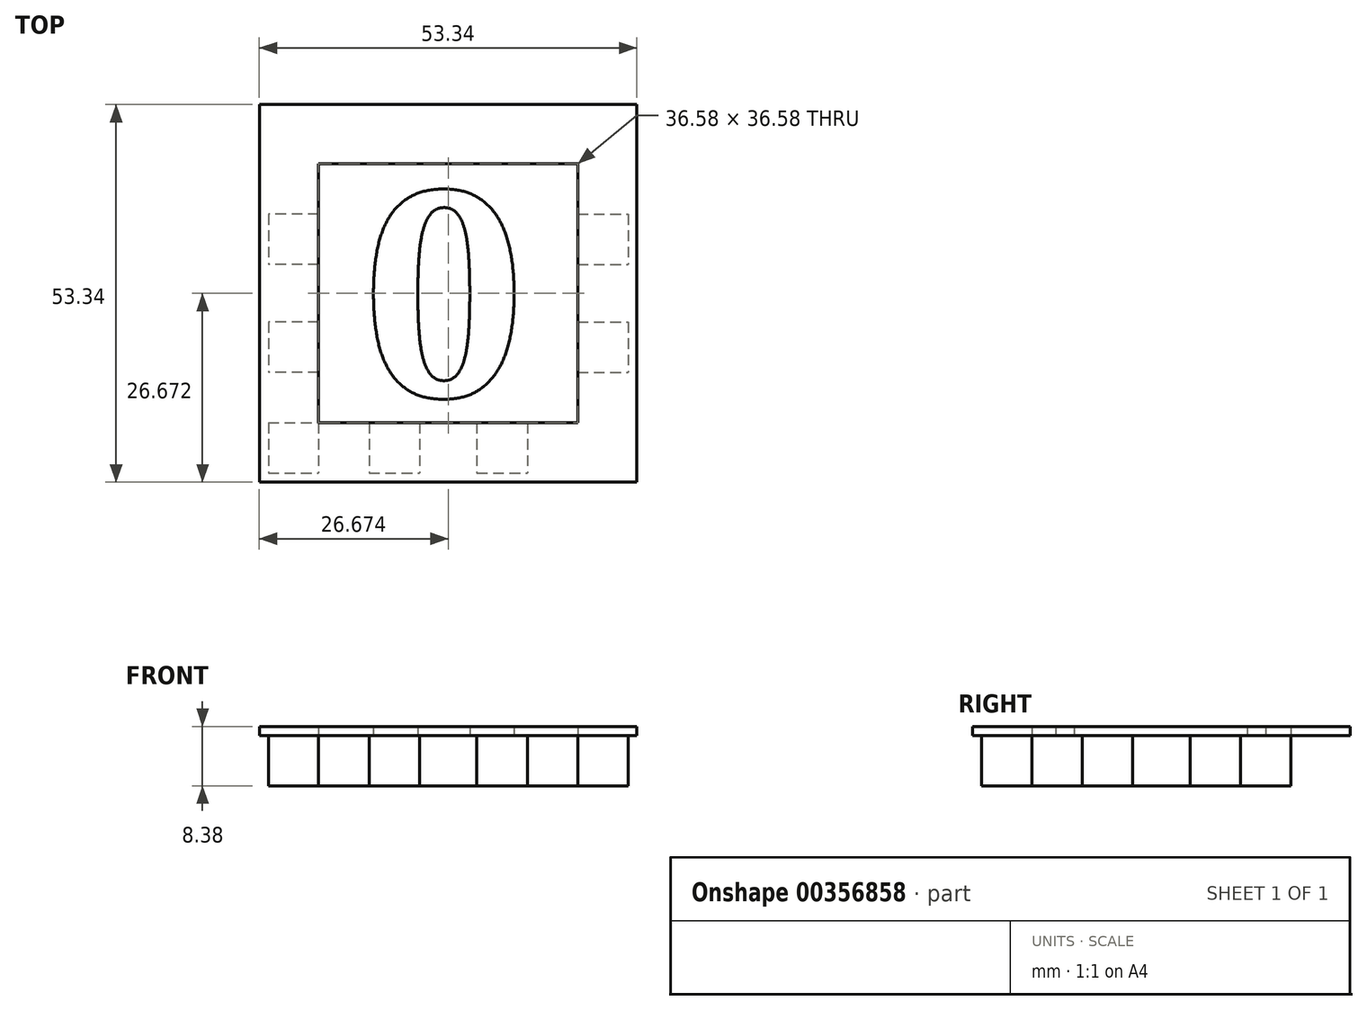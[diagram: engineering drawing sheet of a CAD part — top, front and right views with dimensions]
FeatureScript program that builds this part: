
annotation { "Feature Type Name" : "Feature", "Feature Type Description" : "" }
export const myFeature = defineFeature(function(context is Context, id is Id, definition is map)
    precondition{}
    {
        {
            var Q0;
            Q0=qCreatedBy(makeId("Top.planeOp"),FACE);
            var sketch = newSketch(context, id + "F0", { "sketchPlane" : qUnion([Q0])});
            skLineSegment(sketch, "E0.bottom", {"start": v(-28.29, 26.77) * mm, "end": v(15.4, 26.77) * mm});
            skLineSegment(sketch, "E0.top", {"start": v(-28.29, -24.03) * mm, "end": v(15.4, -24.03) * mm});
            skLineSegment(sketch, "E0.left", {"start": v(-28.29, 26.77) * mm, "end": v(-28.29, -24.03) * mm});
            skLineSegment(sketch, "E0.right", {"start": v(15.4, 26.77) * mm, "end": v(15.4, -24.03) * mm});
            skLineSegment(sketch, "E1.bottom", {"start": v(-28.29, 26.77) * mm, "end": v(-21.17, 26.77) * mm});
            skLineSegment(sketch, "E1.top", {"start": v(-28.29, 19.66) * mm, "end": v(-21.17, 19.66) * mm});
            skLineSegment(sketch, "E1.left", {"start": v(-28.29, 26.77) * mm, "end": v(-28.29, 19.66) * mm});
            skLineSegment(sketch, "E1.right", {"start": v(-21.17, 26.77) * mm, "end": v(-21.17, 19.66) * mm});
            skLineSegment(sketch, "E2.bottom", {"start": v(-21.17, 26.77) * mm, "end": v(-14.06, 26.77) * mm});
            skLineSegment(sketch, "E2.top", {"start": v(-21.17, 19.66) * mm, "end": v(-14.06, 19.66) * mm});
            skLineSegment(sketch, "E2.right", {"start": v(-14.06, 26.77) * mm, "end": v(-14.06, 19.66) * mm});
            skLineSegment(sketch, "E3.bottom", {"start": v(-14.06, 26.77) * mm, "end": v(-6.95, 26.77) * mm});
            skLineSegment(sketch, "E3.top", {"start": v(-14.06, 19.66) * mm, "end": v(-6.95, 19.66) * mm});
            skLineSegment(sketch, "E3.right", {"start": v(-6.95, 26.77) * mm, "end": v(-6.95, 19.66) * mm});
            skLineSegment(sketch, "E4.bottom", {"start": v(-6.95, 26.77) * mm, "end": v(1.18, 26.77) * mm});
            skLineSegment(sketch, "E4.top", {"start": v(-6.95, 19.66) * mm, "end": v(1.18, 19.66) * mm});
            skLineSegment(sketch, "E4.right", {"start": v(1.18, 26.77) * mm, "end": v(1.18, 19.66) * mm});
            skLineSegment(sketch, "E5.bottom", {"start": v(1.18, 26.77) * mm, "end": v(8.3, 26.77) * mm});
            skLineSegment(sketch, "E5.top", {"start": v(1.18, 19.66) * mm, "end": v(8.3, 19.66) * mm});
            skLineSegment(sketch, "E5.right", {"start": v(8.3, 26.77) * mm, "end": v(8.3, 19.66) * mm});
            skLineSegment(sketch, "E6.bottom", {"start": v(8.3, 26.77) * mm, "end": v(22.51, 26.77) * mm});
            skLineSegment(sketch, "E6.top", {"start": v(8.3, 19.66) * mm, "end": v(22.51, 19.66) * mm});
            skLineSegment(sketch, "E6.right", {"start": v(22.51, 26.77) * mm, "end": v(22.51, 19.66) * mm});
            skLineSegment(sketch, "E7.bottom", {"start": v(15.4, 26.77) * mm, "end": v(22.51, 26.77) * mm});
            skLineSegment(sketch, "E7.top", {"start": v(15.4, 19.66) * mm, "end": v(22.51, 19.66) * mm});
            skLineSegment(sketch, "E7.right", {"start": v(15.4, 26.77) * mm, "end": v(15.4, 19.66) * mm});
            skLineSegment(sketch, "E8.top", {"start": v(15.4, 12.55) * mm, "end": v(22.51, 12.55) * mm});
            skLineSegment(sketch, "E8.left", {"start": v(22.51, 19.66) * mm, "end": v(22.51, 12.55) * mm});
            skLineSegment(sketch, "E8.right", {"start": v(15.4, 19.66) * mm, "end": v(15.4, 12.55) * mm});
            skLineSegment(sketch, "E9.top", {"start": v(15.4, 5.44) * mm, "end": v(22.51, 5.44) * mm});
            skLineSegment(sketch, "E9.left", {"start": v(22.51, 12.55) * mm, "end": v(22.51, 5.44) * mm});
            skLineSegment(sketch, "E9.right", {"start": v(15.4, 12.55) * mm, "end": v(15.4, 5.44) * mm});
            skLineSegment(sketch, "E10.top", {"start": v(15.4, -2.7) * mm, "end": v(22.51, -2.7) * mm});
            skLineSegment(sketch, "E10.left", {"start": v(22.51, 5.44) * mm, "end": v(22.51, -2.7) * mm});
            skLineSegment(sketch, "E10.right", {"start": v(15.4, 5.44) * mm, "end": v(15.4, -2.7) * mm});
            skLineSegment(sketch, "E11.top", {"start": v(15.4, -9.8) * mm, "end": v(22.51, -9.8) * mm});
            skLineSegment(sketch, "E11.left", {"start": v(22.51, -2.7) * mm, "end": v(22.51, -9.8) * mm});
            skLineSegment(sketch, "E11.right", {"start": v(15.4, -2.7) * mm, "end": v(15.4, -9.8) * mm});
            skLineSegment(sketch, "E12.top", {"start": v(15.4, -16.92) * mm, "end": v(22.51, -16.92) * mm});
            skLineSegment(sketch, "E12.left", {"start": v(22.51, -9.8) * mm, "end": v(22.51, -16.92) * mm});
            skLineSegment(sketch, "E12.right", {"start": v(15.4, -9.8) * mm, "end": v(15.4, -16.92) * mm});
            skLineSegment(sketch, "E13.top", {"start": v(15.4, -24.03) * mm, "end": v(22.51, -24.03) * mm});
            skLineSegment(sketch, "E13.left", {"start": v(22.51, -16.92) * mm, "end": v(22.51, -24.03) * mm});
            skLineSegment(sketch, "E13.right", {"start": v(15.4, -16.92) * mm, "end": v(15.4, -24.03) * mm});
            skLineSegment(sketch, "E14.bottom", {"start": v(22.51, -16.92) * mm, "end": v(8.3, -16.92) * mm});
            skLineSegment(sketch, "E14.top", {"start": v(22.51, -24.03) * mm, "end": v(8.3, -24.03) * mm});
            skLineSegment(sketch, "E14.right", {"start": v(8.3, -16.92) * mm, "end": v(8.3, -24.03) * mm});
            skLineSegment(sketch, "E15.bottom", {"start": v(8.3, -16.92) * mm, "end": v(1.18, -16.92) * mm});
            skLineSegment(sketch, "E15.top", {"start": v(8.3, -24.03) * mm, "end": v(1.18, -24.03) * mm});
            skLineSegment(sketch, "E15.right", {"start": v(1.18, -16.92) * mm, "end": v(1.18, -24.03) * mm});
            skLineSegment(sketch, "E16.bottom", {"start": v(1.18, -16.92) * mm, "end": v(-6.95, -16.92) * mm});
            skLineSegment(sketch, "E16.top", {"start": v(1.18, -24.03) * mm, "end": v(-6.95, -24.03) * mm});
            skLineSegment(sketch, "E16.right", {"start": v(-6.95, -16.92) * mm, "end": v(-6.95, -24.03) * mm});
            skLineSegment(sketch, "E17.bottom", {"start": v(-6.95, -16.92) * mm, "end": v(-14.06, -16.92) * mm});
            skLineSegment(sketch, "E17.top", {"start": v(-6.95, -24.03) * mm, "end": v(-14.06, -24.03) * mm});
            skLineSegment(sketch, "E17.right", {"start": v(-14.06, -16.92) * mm, "end": v(-14.06, -24.03) * mm});
            skLineSegment(sketch, "E18.bottom", {"start": v(-21.17, 19.66) * mm, "end": v(-28.29, 19.66) * mm});
            skLineSegment(sketch, "E18.top", {"start": v(-21.17, 12.55) * mm, "end": v(-28.29, 12.55) * mm});
            skLineSegment(sketch, "E18.left", {"start": v(-21.17, 19.66) * mm, "end": v(-21.17, 12.55) * mm});
            skLineSegment(sketch, "E18.right", {"start": v(-28.29, 19.66) * mm, "end": v(-28.29, 12.55) * mm});
            skLineSegment(sketch, "E19.top", {"start": v(-21.17, 5.44) * mm, "end": v(-28.29, 5.44) * mm});
            skLineSegment(sketch, "E19.left", {"start": v(-21.17, 12.55) * mm, "end": v(-21.17, 5.44) * mm});
            skLineSegment(sketch, "E19.right", {"start": v(-28.29, 12.55) * mm, "end": v(-28.29, 5.44) * mm});
            skLineSegment(sketch, "E20.top", {"start": v(-21.17, -2.7) * mm, "end": v(-28.29, -2.7) * mm});
            skLineSegment(sketch, "E20.left", {"start": v(-21.17, 5.44) * mm, "end": v(-21.17, -2.7) * mm});
            skLineSegment(sketch, "E20.right", {"start": v(-28.29, 5.44) * mm, "end": v(-28.29, -2.7) * mm});
            skLineSegment(sketch, "E21.top", {"start": v(-21.17, -9.8) * mm, "end": v(-28.29, -9.8) * mm});
            skLineSegment(sketch, "E21.left", {"start": v(-21.17, -2.7) * mm, "end": v(-21.17, -9.8) * mm});
            skLineSegment(sketch, "E21.right", {"start": v(-28.29, -2.7) * mm, "end": v(-28.29, -9.8) * mm});
            skLineSegment(sketch, "E22.bottom", {"start": v(-28.29, -9.8) * mm, "end": v(-21.17, -9.8) * mm});
            skLineSegment(sketch, "E22.top", {"start": v(-28.29, -16.92) * mm, "end": v(-21.17, -16.92) * mm});
            skLineSegment(sketch, "E22.left", {"start": v(-28.29, -9.8) * mm, "end": v(-28.29, -16.92) * mm});
            skLineSegment(sketch, "E22.right", {"start": v(-21.17, -9.8) * mm, "end": v(-21.17, -16.92) * mm});
            skLineSegment(sketch, "E23.top", {"start": v(-28.29, -24.03) * mm, "end": v(-21.17, -24.03) * mm});
            skLineSegment(sketch, "E23.left", {"start": v(-28.29, -16.92) * mm, "end": v(-28.29, -24.03) * mm});
            skLineSegment(sketch, "E23.right", {"start": v(-21.17, -16.92) * mm, "end": v(-21.17, -24.03) * mm});
            skLineSegment(sketch, "E24.bottom", {"start": v(-21.17, -16.92) * mm, "end": v(-14.06, -16.92) * mm});
            skLineSegment(sketch, "E24.top", {"start": v(-21.17, -24.03) * mm, "end": v(-14.06, -24.03) * mm});
            skLineSegment(sketch, "E25.bottom", {"start": v(55.44, 26.09) * mm, "end": v(106.24, 26.09) * mm});
            skLineSegment(sketch, "E25.top", {"start": v(55.44, -24.71) * mm, "end": v(106.24, -24.71) * mm});
            skLineSegment(sketch, "E25.left", {"start": v(55.44, 26.09) * mm, "end": v(55.44, -24.71) * mm});
            skLineSegment(sketch, "E25.right", {"start": v(106.24, 26.09) * mm, "end": v(106.24, -24.71) * mm});
            skLineSegment(sketch, "E26.bottom", {"start": v(55.44, 26.09) * mm, "end": v(62.55, 26.09) * mm});
            skLineSegment(sketch, "E26.top", {"start": v(55.44, 18.97) * mm, "end": v(62.55, 18.97) * mm});
            skLineSegment(sketch, "E26.left", {"start": v(55.44, 26.09) * mm, "end": v(55.44, 18.97) * mm});
            skLineSegment(sketch, "E26.right", {"start": v(62.55, 26.09) * mm, "end": v(62.55, 18.97) * mm});
            skLineSegment(sketch, "E27.bottom", {"start": v(62.55, 26.09) * mm, "end": v(69.67, 26.09) * mm});
            skLineSegment(sketch, "E27.top", {"start": v(62.55, 18.97) * mm, "end": v(69.67, 18.97) * mm});
            skLineSegment(sketch, "E27.right", {"start": v(69.67, 26.09) * mm, "end": v(69.67, 18.97) * mm});
            skLineSegment(sketch, "E28.bottom", {"start": v(69.67, 26.09) * mm, "end": v(76.78, 26.09) * mm});
            skLineSegment(sketch, "E28.top", {"start": v(69.67, 18.97) * mm, "end": v(76.78, 18.97) * mm});
            skLineSegment(sketch, "E28.right", {"start": v(76.78, 26.09) * mm, "end": v(76.78, 18.97) * mm});
            skLineSegment(sketch, "E29.bottom", {"start": v(76.78, 26.09) * mm, "end": v(84.9, 26.09) * mm});
            skLineSegment(sketch, "E29.top", {"start": v(76.78, 18.97) * mm, "end": v(84.9, 18.97) * mm});
            skLineSegment(sketch, "E29.right", {"start": v(84.9, 26.09) * mm, "end": v(84.9, 18.97) * mm});
            skLineSegment(sketch, "E30.bottom", {"start": v(84.9, 26.09) * mm, "end": v(92.02, 26.09) * mm});
            skLineSegment(sketch, "E30.top", {"start": v(84.9, 18.97) * mm, "end": v(92.02, 18.97) * mm});
            skLineSegment(sketch, "E30.right", {"start": v(92.02, 26.09) * mm, "end": v(92.02, 18.97) * mm});
            skLineSegment(sketch, "E31.bottom", {"start": v(92.02, 26.09) * mm, "end": v(99.13, 26.09) * mm});
            skLineSegment(sketch, "E31.top", {"start": v(92.02, 18.97) * mm, "end": v(99.13, 18.97) * mm});
            skLineSegment(sketch, "E31.right", {"start": v(99.13, 26.09) * mm, "end": v(99.13, 18.97) * mm});
            skLineSegment(sketch, "E32.bottom", {"start": v(99.13, 26.09) * mm, "end": v(106.24, 26.09) * mm});
            skLineSegment(sketch, "E32.top", {"start": v(99.13, 18.97) * mm, "end": v(106.24, 18.97) * mm});
            skLineSegment(sketch, "E32.right", {"start": v(106.24, 26.09) * mm, "end": v(106.24, 18.97) * mm});
            skLineSegment(sketch, "E33.top", {"start": v(99.13, 11.86) * mm, "end": v(106.24, 11.86) * mm});
            skLineSegment(sketch, "E33.left", {"start": v(99.13, 18.97) * mm, "end": v(99.13, 11.86) * mm});
            skLineSegment(sketch, "E33.right", {"start": v(106.24, 18.97) * mm, "end": v(106.24, 11.86) * mm});
            skLineSegment(sketch, "E34.top", {"start": v(99.13, 4.75) * mm, "end": v(106.24, 4.75) * mm});
            skLineSegment(sketch, "E34.left", {"start": v(99.13, 11.86) * mm, "end": v(99.13, 4.75) * mm});
            skLineSegment(sketch, "E34.right", {"start": v(106.24, 11.86) * mm, "end": v(106.24, 4.75) * mm});
            skLineSegment(sketch, "E35.top", {"start": v(99.13, -3.38) * mm, "end": v(106.24, -3.38) * mm});
            skLineSegment(sketch, "E35.left", {"start": v(99.13, 4.75) * mm, "end": v(99.13, -3.38) * mm});
            skLineSegment(sketch, "E35.right", {"start": v(106.24, 4.75) * mm, "end": v(106.24, -3.38) * mm});
            skLineSegment(sketch, "E36.top", {"start": v(99.13, -10.49) * mm, "end": v(106.24, -10.49) * mm});
            skLineSegment(sketch, "E36.left", {"start": v(99.13, -3.38) * mm, "end": v(99.13, -10.49) * mm});
            skLineSegment(sketch, "E36.right", {"start": v(106.24, -3.38) * mm, "end": v(106.24, -10.49) * mm});
            skLineSegment(sketch, "E37.top", {"start": v(99.13, -17.6) * mm, "end": v(106.24, -17.6) * mm});
            skLineSegment(sketch, "E37.left", {"start": v(99.13, -10.49) * mm, "end": v(99.13, -17.6) * mm});
            skLineSegment(sketch, "E37.right", {"start": v(106.24, -10.49) * mm, "end": v(106.24, -17.6) * mm});
            skLineSegment(sketch, "E38.top", {"start": v(99.13, -24.71) * mm, "end": v(106.24, -24.71) * mm});
            skLineSegment(sketch, "E38.left", {"start": v(99.13, -17.6) * mm, "end": v(99.13, -24.71) * mm});
            skLineSegment(sketch, "E38.right", {"start": v(106.24, -17.6) * mm, "end": v(106.24, -24.71) * mm});
            skLineSegment(sketch, "E39.bottom", {"start": v(99.13, -17.6) * mm, "end": v(92.02, -17.6) * mm});
            skLineSegment(sketch, "E39.top", {"start": v(99.13, -24.71) * mm, "end": v(92.02, -24.71) * mm});
            skLineSegment(sketch, "E39.right", {"start": v(92.02, -17.6) * mm, "end": v(92.02, -24.71) * mm});
            skLineSegment(sketch, "E40.bottom", {"start": v(92.02, -17.6) * mm, "end": v(84.9, -17.6) * mm});
            skLineSegment(sketch, "E40.top", {"start": v(92.02, -24.71) * mm, "end": v(84.9, -24.71) * mm});
            skLineSegment(sketch, "E40.right", {"start": v(84.9, -17.6) * mm, "end": v(84.9, -24.71) * mm});
            skLineSegment(sketch, "E41.bottom", {"start": v(84.9, -17.6) * mm, "end": v(76.78, -17.6) * mm});
            skLineSegment(sketch, "E41.top", {"start": v(84.9, -24.71) * mm, "end": v(76.78, -24.71) * mm});
            skLineSegment(sketch, "E41.right", {"start": v(76.78, -17.6) * mm, "end": v(76.78, -24.71) * mm});
            skLineSegment(sketch, "E42.bottom", {"start": v(76.78, -17.6) * mm, "end": v(69.67, -17.6) * mm});
            skLineSegment(sketch, "E42.top", {"start": v(76.78, -24.71) * mm, "end": v(69.67, -24.71) * mm});
            skLineSegment(sketch, "E42.right", {"start": v(69.67, -17.6) * mm, "end": v(69.67, -24.71) * mm});
            skLineSegment(sketch, "E43.bottom", {"start": v(62.55, 18.97) * mm, "end": v(55.44, 18.97) * mm});
            skLineSegment(sketch, "E43.top", {"start": v(62.55, 11.86) * mm, "end": v(55.44, 11.86) * mm});
            skLineSegment(sketch, "E43.left", {"start": v(62.55, 18.97) * mm, "end": v(62.55, 11.86) * mm});
            skLineSegment(sketch, "E43.right", {"start": v(55.44, 18.97) * mm, "end": v(55.44, 11.86) * mm});
            skLineSegment(sketch, "E44.top", {"start": v(62.55, 4.75) * mm, "end": v(55.44, 4.75) * mm});
            skLineSegment(sketch, "E44.left", {"start": v(62.55, 11.86) * mm, "end": v(62.55, 4.75) * mm});
            skLineSegment(sketch, "E44.right", {"start": v(55.44, 11.86) * mm, "end": v(55.44, 4.75) * mm});
            skLineSegment(sketch, "E45.top", {"start": v(62.55, -3.38) * mm, "end": v(55.44, -3.38) * mm});
            skLineSegment(sketch, "E45.left", {"start": v(62.55, 4.75) * mm, "end": v(62.55, -3.38) * mm});
            skLineSegment(sketch, "E45.right", {"start": v(55.44, 4.75) * mm, "end": v(55.44, -3.38) * mm});
            skLineSegment(sketch, "E46.top", {"start": v(62.55, -10.49) * mm, "end": v(55.44, -10.49) * mm});
            skLineSegment(sketch, "E46.left", {"start": v(62.55, -3.38) * mm, "end": v(62.55, -10.49) * mm});
            skLineSegment(sketch, "E46.right", {"start": v(55.44, -3.38) * mm, "end": v(55.44, -10.49) * mm});
            skLineSegment(sketch, "E47.top", {"start": v(62.55, -17.6) * mm, "end": v(55.44, -17.6) * mm});
            skLineSegment(sketch, "E47.left", {"start": v(62.55, -10.49) * mm, "end": v(62.55, -17.6) * mm});
            skLineSegment(sketch, "E47.right", {"start": v(55.44, -10.49) * mm, "end": v(55.44, -17.6) * mm});
            skLineSegment(sketch, "E48.bottom", {"start": v(62.55, -17.6) * mm, "end": v(69.67, -17.6) * mm});
            skLineSegment(sketch, "E48.top", {"start": v(62.55, -24.71) * mm, "end": v(69.67, -24.71) * mm});
            skLineSegment(sketch, "E48.left", {"start": v(62.55, -17.6) * mm, "end": v(62.55, -24.71) * mm});
            skLineSegment(sketch, "E49.top", {"start": v(62.55, -24.71) * mm, "end": v(55.44, -24.71) * mm});
            skLineSegment(sketch, "E49.right", {"start": v(55.44, -17.6) * mm, "end": v(55.44, -24.71) * mm});
            skSolve(sketch);
        }
        {
            var Q0;
            Q0=makeQuery(id+"F0.imprint","IMPRINT",FACE,{"disambiguationData":[TD([[makeQuery(id+"F0.imprint","IMPRINT",EDGE,{"derivedFrom":sQuery(id+"F0.wireOp",EDGE,"E1.bottom")}),-1.0]])]});
            var Q1;
            Q1=makeQuery(id+"F0.imprint","IMPRINT",FACE,{"disambiguationData":[TD([[makeQuery(id+"F0.imprint","IMPRINT",EDGE,{"derivedFrom":sQuery(id+"F0.wireOp",EDGE,"E3.bottom")}),-1.0]])]});
            var Q2;
            Q2=makeQuery(id+"F0.imprint","IMPRINT",FACE,{"disambiguationData":[TD([[makeQuery(id+"F0.imprint","IMPRINT",EDGE,{"derivedFrom":sQuery(id+"F0.wireOp",EDGE,"E5.bottom")}),-1.0]])]});
            var Q3;
            Q3=makeQuery(id+"F0.imprint","IMPRINT",FACE,{"disambiguationData":[TD([[makeQuery(id+"F0.imprint","IMPRINT",EDGE,{"derivedFrom":sQuery(id+"F0.wireOp",EDGE,"E7.bottom")}),-1.0]])]});
            var Q4;
            Q4=makeQuery(id+"F0.imprint","IMPRINT",FACE,{"disambiguationData":[TD([[makeQuery(id+"F0.imprint","IMPRINT",EDGE,{"derivedFrom":sQuery(id+"F0.wireOp",EDGE,"E8.top")}),-1.0]])]});
            var Q5;
            Q5=makeQuery(id+"F0.imprint","IMPRINT",FACE,{"disambiguationData":[TD([[makeQuery(id+"F0.imprint","IMPRINT",EDGE,{"derivedFrom":sQuery(id+"F0.wireOp",EDGE,"E10.top")}),-1.0]])]});
            var Q6;
            {var subQ0=sQuery(id+"F0.wireOp",EDGE,"E13.right");Q6=makeQuery(id+"F0.imprint","IMPRINT",FACE,{"disambiguationData":[TD([[makeQuery(id+"F0.imprint","IMPRINT",EDGE,{"derivedFrom":subQ0}),1.0]])]});}
            var Q7;
            Q7=makeQuery(id+"F0.imprint","IMPRINT",FACE,{"disambiguationData":[TD([[makeQuery(id+"F0.imprint","IMPRINT",EDGE,{"derivedFrom":sQuery(id+"F0.wireOp",EDGE,"E15.bottom")}),1.0]])]});
            var Q8;
            Q8=makeQuery(id+"F0.imprint","IMPRINT",FACE,{"disambiguationData":[TD([[makeQuery(id+"F0.imprint","IMPRINT",EDGE,{"derivedFrom":sQuery(id+"F0.wireOp",EDGE,"E2.top")}),-1.0]])]});
            var Q9;
            Q9=makeQuery(id+"F0.imprint","IMPRINT",FACE,{"disambiguationData":[TD([[makeQuery(id+"F0.imprint","IMPRINT",EDGE,{"derivedFrom":sQuery(id+"F0.wireOp",EDGE,"E17.bottom")}),1.0]])]});
            var Q10;
            Q10=makeQuery(id+"F0.imprint","IMPRINT",FACE,{"disambiguationData":[TD([[makeQuery(id+"F0.imprint","IMPRINT",EDGE,{"derivedFrom":sQuery(id+"F0.wireOp",EDGE,"E22.top")}),-1.0]])]});
            var Q11;
            Q11=makeQuery(id+"F0.imprint","IMPRINT",FACE,{"disambiguationData":[TD([[makeQuery(id+"F0.imprint","IMPRINT",EDGE,{"derivedFrom":sQuery(id+"F0.wireOp",EDGE,"E20.top")}),1.0]])]});
            var Q12;
            Q12=makeQuery(id+"F0.imprint","IMPRINT",FACE,{"disambiguationData":[TD([[makeQuery(id+"F0.imprint","IMPRINT",EDGE,{"derivedFrom":sQuery(id+"F0.wireOp",EDGE,"E18.top")}),1.0]])]});
            var Q13;
            Q13=makeQuery(id+"F0.imprint","IMPRINT",FACE,{"disambiguationData":[TD([[makeQuery(id+"F0.imprint","IMPRINT",EDGE,{"derivedFrom":sQuery(id+"F0.wireOp",EDGE,"E27.top")}),-1.0]])]});
            var Q14;
            Q14=makeQuery(id+"F0.imprint","IMPRINT",FACE,{"disambiguationData":[TD([[makeQuery(id+"F0.imprint","IMPRINT",EDGE,{"derivedFrom":sQuery(id+"F0.wireOp",EDGE,"E31.bottom")}),-1.0]])]});
            var Q15;
            Q15=makeQuery(id+"F0.imprint","IMPRINT",FACE,{"disambiguationData":[TD([[makeQuery(id+"F0.imprint","IMPRINT",EDGE,{"derivedFrom":sQuery(id+"F0.wireOp",EDGE,"E29.bottom")}),-1.0]])]});
            var Q16;
            Q16=makeQuery(id+"F0.imprint","IMPRINT",FACE,{"disambiguationData":[TD([[makeQuery(id+"F0.imprint","IMPRINT",EDGE,{"derivedFrom":sQuery(id+"F0.wireOp",EDGE,"E43.bottom")}),1.0]])]});
            var Q17;
            Q17=makeQuery(id+"F0.imprint","IMPRINT",FACE,{"disambiguationData":[TD([[makeQuery(id+"F0.imprint","IMPRINT",EDGE,{"derivedFrom":sQuery(id+"F0.wireOp",EDGE,"E44.top")}),1.0]])]});
            var Q18;
            Q18=makeQuery(id+"F0.imprint","IMPRINT",FACE,{"disambiguationData":[TD([[makeQuery(id+"F0.imprint","IMPRINT",EDGE,{"derivedFrom":sQuery(id+"F0.wireOp",EDGE,"E36.top")}),-1.0]])]});
            var Q19;
            Q19=makeQuery(id+"F0.imprint","IMPRINT",FACE,{"disambiguationData":[TD([[makeQuery(id+"F0.imprint","IMPRINT",EDGE,{"derivedFrom":sQuery(id+"F0.wireOp",EDGE,"E34.top")}),-1.0]])]});
            var Q20;
            Q20=makeQuery(id+"F0.imprint","IMPRINT",FACE,{"disambiguationData":[TD([[makeQuery(id+"F0.imprint","IMPRINT",EDGE,{"derivedFrom":sQuery(id+"F0.wireOp",EDGE,"E46.top")}),1.0]])]});
            var Q21;
            Q21=makeQuery(id+"F0.imprint","IMPRINT",FACE,{"disambiguationData":[TD([[makeQuery(id+"F0.imprint","IMPRINT",EDGE,{"derivedFrom":sQuery(id+"F0.wireOp",EDGE,"E32.top")}),-1.0]])]});
            var Q22;
            Q22=makeQuery(id+"F0.imprint","IMPRINT",FACE,{"disambiguationData":[TD([[makeQuery(id+"F0.imprint","IMPRINT",EDGE,{"derivedFrom":sQuery(id+"F0.wireOp",EDGE,"E27.bottom")}),-1.0]])]});
            var Q23;
            Q23=makeQuery(id+"F0.imprint","IMPRINT",FACE,{"disambiguationData":[TD([[makeQuery(id+"F0.imprint","IMPRINT",EDGE,{"derivedFrom":sQuery(id+"F0.wireOp",EDGE,"E42.bottom")}),1.0]])]});
            var Q24;
            Q24=makeQuery(id+"F0.imprint","IMPRINT",FACE,{"disambiguationData":[TD([[makeQuery(id+"F0.imprint","IMPRINT",EDGE,{"derivedFrom":sQuery(id+"F0.wireOp",EDGE,"E40.bottom")}),1.0]])]});
            extrude(context, id + "F1", {"entities" : qUnion([Q0, Q1, Q2, Q3, Q4, Q5, Q6, Q7, Q8, Q9, Q10, Q11, Q12, Q13, Q14, Q15, Q16, Q17, Q18, Q19, Q20, Q21, Q22, Q23, Q24]), "depth" : 7.11 * mm});
        }
        {
            var Q0;
            Q0=makeQuery(id+"F1.opExtrude","CAP_FACE",FACE,{"disambiguationData":[OSD([sQuery(id+"F0.wireOp",EDGE,"E2.top"),sQuery(id+"F0.wireOp",EDGE,"E3.bottom"),sQuery(id+"F0.wireOp",EDGE,"E2.right"),sQuery(id+"F0.wireOp",EDGE,"E4.top"),sQuery(id+"F0.wireOp",EDGE,"E3.right"),sQuery(id+"F0.wireOp",EDGE,"E5.bottom"),sQuery(id+"F0.wireOp",EDGE,"E4.right"),sQuery(id+"F0.wireOp",EDGE,"E6.top"),sQuery(id+"F0.wireOp",EDGE,"E5.right"),sQuery(id+"F0.wireOp",EDGE,"E8.right"),sQuery(id+"F0.wireOp",EDGE,"E8.top"),sQuery(id+"F0.wireOp",EDGE,"E9.left"),sQuery(id+"F0.wireOp",EDGE,"E9.top"),sQuery(id+"F0.wireOp",EDGE,"E10.right"),sQuery(id+"F0.wireOp",EDGE,"E10.top"),sQuery(id+"F0.wireOp",EDGE,"E11.left"),sQuery(id+"F0.wireOp",EDGE,"E11.top"),sQuery(id+"F0.wireOp",EDGE,"E12.right"),sQuery(id+"F0.wireOp",EDGE,"E14.bottom"),sQuery(id+"F0.wireOp",EDGE,"E15.top"),sQuery(id+"F0.wireOp",EDGE,"E14.right"),sQuery(id+"F0.wireOp",EDGE,"E16.bottom"),sQuery(id+"F0.wireOp",EDGE,"E15.right"),sQuery(id+"F0.wireOp",EDGE,"E17.top"),sQuery(id+"F0.wireOp",EDGE,"E16.right"),sQuery(id+"F0.wireOp",EDGE,"E18.left"),sQuery(id+"F0.wireOp",EDGE,"E18.top"),sQuery(id+"F0.wireOp",EDGE,"E19.right"),sQuery(id+"F0.wireOp",EDGE,"E19.top"),sQuery(id+"F0.wireOp",EDGE,"E20.left"),sQuery(id+"F0.wireOp",EDGE,"E20.top"),sQuery(id+"F0.wireOp",EDGE,"E21.right"),sQuery(id+"F0.wireOp",EDGE,"E22.bottom"),sQuery(id+"F0.wireOp",EDGE,"E22.right"),sQuery(id+"F0.wireOp",EDGE,"E24.bottom"),sQuery(id+"F0.wireOp",EDGE,"E17.right")])],"isStart":false});
            var sketch = newSketch(context, id + "F2", { "sketchPlane" : qUnion([Q0])});
            skLineSegment(sketch, "E50.bottom", {"start": v(-29.56, -25.3) * mm, "end": v(23.78, -25.3) * mm});
            skLineSegment(sketch, "E50.top", {"start": v(-29.56, -16.92) * mm, "end": v(23.78, -16.92) * mm});
            skLineSegment(sketch, "E50.left", {"start": v(-29.56, -25.3) * mm, "end": v(-29.56, -16.92) * mm});
            skLineSegment(sketch, "E50.right", {"start": v(23.78, -25.3) * mm, "end": v(23.78, -16.92) * mm});
            skLineSegment(sketch, "E51.bottom", {"start": v(-29.56, -25.3) * mm, "end": v(-21.17, -25.3) * mm});
            skLineSegment(sketch, "E51.top", {"start": v(-29.56, 28.04) * mm, "end": v(-21.17, 28.04) * mm});
            skLineSegment(sketch, "E51.left", {"start": v(-29.56, -25.3) * mm, "end": v(-29.56, 28.04) * mm});
            skLineSegment(sketch, "E51.right", {"start": v(-21.17, -25.3) * mm, "end": v(-21.17, 28.04) * mm});
            skLineSegment(sketch, "E52.bottom", {"start": v(-29.56, 19.66) * mm, "end": v(23.78, 19.66) * mm});
            skLineSegment(sketch, "E52.top", {"start": v(-29.56, 28.04) * mm, "end": v(23.78, 28.04) * mm});
            skLineSegment(sketch, "E52.left", {"start": v(-29.56, 19.66) * mm, "end": v(-29.56, 28.04) * mm});
            skLineSegment(sketch, "E52.right", {"start": v(23.78, 19.66) * mm, "end": v(23.78, 28.04) * mm});
            skLineSegment(sketch, "E53.bottom", {"start": v(23.78, 28.04) * mm, "end": v(15.4, 28.04) * mm});
            skLineSegment(sketch, "E53.top", {"start": v(23.78, -25.3) * mm, "end": v(15.4, -25.3) * mm});
            skLineSegment(sketch, "E53.left", {"start": v(23.78, 28.04) * mm, "end": v(23.78, -25.3) * mm});
            skLineSegment(sketch, "E53.right", {"start": v(15.4, 28.04) * mm, "end": v(15.4, -25.3) * mm});
            skSolve(sketch);
        }
        {
            var Q0;
            Q0=qSketchRegion(id+"F2",true);
            extrude(context, id + "F3", {"entities" : qUnion([Q0]), "depth" : 1.27 * mm});
        }
        {
            var Q0;
            Q0=makeQuery(id+"F1.opExtrude","CAP_FACE",FACE,{"disambiguationData":[OSD([sQuery(id+"F0.wireOp",EDGE,"E27.bottom"),sQuery(id+"F0.wireOp",EDGE,"E26.right"),sQuery(id+"F0.wireOp",EDGE,"E28.top"),sQuery(id+"F0.wireOp",EDGE,"E27.right"),sQuery(id+"F0.wireOp",EDGE,"E29.bottom"),sQuery(id+"F0.wireOp",EDGE,"E28.right"),sQuery(id+"F0.wireOp",EDGE,"E30.top"),sQuery(id+"F0.wireOp",EDGE,"E29.right"),sQuery(id+"F0.wireOp",EDGE,"E31.bottom"),sQuery(id+"F0.wireOp",EDGE,"E30.right"),sQuery(id+"F0.wireOp",EDGE,"E31.right"),sQuery(id+"F0.wireOp",EDGE,"E32.top"),sQuery(id+"F0.wireOp",EDGE,"E33.right"),sQuery(id+"F0.wireOp",EDGE,"E33.top"),sQuery(id+"F0.wireOp",EDGE,"E34.left"),sQuery(id+"F0.wireOp",EDGE,"E34.top"),sQuery(id+"F0.wireOp",EDGE,"E35.right"),sQuery(id+"F0.wireOp",EDGE,"E35.top"),sQuery(id+"F0.wireOp",EDGE,"E36.left"),sQuery(id+"F0.wireOp",EDGE,"E36.top"),sQuery(id+"F0.wireOp",EDGE,"E37.right"),sQuery(id+"F0.wireOp",EDGE,"E37.top"),sQuery(id+"F0.wireOp",EDGE,"E39.bottom"),sQuery(id+"F0.wireOp",EDGE,"E40.top"),sQuery(id+"F0.wireOp",EDGE,"E39.right"),sQuery(id+"F0.wireOp",EDGE,"E41.bottom"),sQuery(id+"F0.wireOp",EDGE,"E40.right"),sQuery(id+"F0.wireOp",EDGE,"E42.top"),sQuery(id+"F0.wireOp",EDGE,"E41.right"),sQuery(id+"F0.wireOp",EDGE,"E43.bottom"),sQuery(id+"F0.wireOp",EDGE,"E43.right"),sQuery(id+"F0.wireOp",EDGE,"E43.top"),sQuery(id+"F0.wireOp",EDGE,"E44.left"),sQuery(id+"F0.wireOp",EDGE,"E44.top"),sQuery(id+"F0.wireOp",EDGE,"E45.right"),sQuery(id+"F0.wireOp",EDGE,"E45.top"),sQuery(id+"F0.wireOp",EDGE,"E46.left"),sQuery(id+"F0.wireOp",EDGE,"E46.top"),sQuery(id+"F0.wireOp",EDGE,"E47.right"),sQuery(id+"F0.wireOp",EDGE,"E48.bottom"),sQuery(id+"F0.wireOp",EDGE,"E42.right"),sQuery(id+"F0.wireOp",EDGE,"E47.top")])],"isStart":false});
            var sketch = newSketch(context, id + "F4", { "sketchPlane" : qUnion([Q0])});
            skLineSegment(sketch, "E54.bottom", {"start": v(55.44, -24.71) * mm, "end": v(62.55, -24.71) * mm});
            skLineSegment(sketch, "E54.top", {"start": v(55.44, 26.09) * mm, "end": v(62.55, 26.09) * mm});
            skLineSegment(sketch, "E54.left", {"start": v(55.44, -24.71) * mm, "end": v(55.44, 26.09) * mm});
            skLineSegment(sketch, "E54.right", {"start": v(62.55, -24.71) * mm, "end": v(62.55, 26.09) * mm});
            skLineSegment(sketch, "E55.bottom", {"start": v(55.44, -24.71) * mm, "end": v(106.24, -24.71) * mm});
            skLineSegment(sketch, "E55.top", {"start": v(55.44, -17.6) * mm, "end": v(106.24, -17.6) * mm});
            skLineSegment(sketch, "E55.left", {"start": v(55.44, -24.71) * mm, "end": v(55.44, -17.6) * mm});
            skLineSegment(sketch, "E55.right", {"start": v(106.24, -24.71) * mm, "end": v(106.24, -17.6) * mm});
            skLineSegment(sketch, "E56.bottom", {"start": v(106.24, -24.71) * mm, "end": v(99.13, -24.71) * mm});
            skLineSegment(sketch, "E56.top", {"start": v(106.24, 26.09) * mm, "end": v(99.13, 26.09) * mm});
            skLineSegment(sketch, "E56.left", {"start": v(106.24, -24.71) * mm, "end": v(106.24, 26.09) * mm});
            skLineSegment(sketch, "E56.right", {"start": v(99.13, -24.71) * mm, "end": v(99.13, 26.09) * mm});
            skLineSegment(sketch, "E57.bottom", {"start": v(106.24, 26.09) * mm, "end": v(55.44, 26.09) * mm});
            skLineSegment(sketch, "E57.top", {"start": v(106.24, 18.97) * mm, "end": v(55.44, 18.97) * mm});
            skLineSegment(sketch, "E57.left", {"start": v(106.24, 26.09) * mm, "end": v(106.24, 18.97) * mm});
            skLineSegment(sketch, "E57.right", {"start": v(55.44, 26.09) * mm, "end": v(55.44, 18.97) * mm});
            skSolve(sketch);
        }
        {
            var Q0;
            Q0=qSketchRegion(id+"F4",true);
            extrude(context, id + "F5", {"entities" : qUnion([Q0]), "depth" : 1.27 * mm});
        }
        {
            var Q0;
            Q0=makeQuery(id+"F5.opExtrude","SWEPT_BODY",BODY,{"disambiguationData":[OSD([sQuery(id+"F4.wireOp",EDGE,"E54.left"),sQuery(id+"F4.wireOp",EDGE,"E54.right"),sQuery(id+"F4.wireOp",EDGE,"E55.bottom"),sQuery(id+"F4.wireOp",EDGE,"E55.top"),sQuery(id+"F4.wireOp",EDGE,"E55.left"),sQuery(id+"F4.wireOp",EDGE,"E56.bottom"),sQuery(id+"F4.wireOp",EDGE,"E56.left"),sQuery(id+"F4.wireOp",EDGE,"E56.right"),sQuery(id+"F4.wireOp",EDGE,"E57.bottom"),sQuery(id+"F4.wireOp",EDGE,"E57.top"),sQuery(id+"F4.wireOp",EDGE,"E57.left"),sQuery(id+"F4.wireOp",EDGE,"E57.right")])]});
            var Q1;
            Q1=makeQuery(id+"F1.opExtrude","SWEPT_BODY",BODY,{"disambiguationData":[OSD([sQuery(id+"F0.wireOp",EDGE,"E27.bottom"),sQuery(id+"F0.wireOp",EDGE,"E26.right"),sQuery(id+"F0.wireOp",EDGE,"E28.top"),sQuery(id+"F0.wireOp",EDGE,"E27.right"),sQuery(id+"F0.wireOp",EDGE,"E29.bottom"),sQuery(id+"F0.wireOp",EDGE,"E28.right"),sQuery(id+"F0.wireOp",EDGE,"E30.top"),sQuery(id+"F0.wireOp",EDGE,"E29.right"),sQuery(id+"F0.wireOp",EDGE,"E31.bottom"),sQuery(id+"F0.wireOp",EDGE,"E30.right"),sQuery(id+"F0.wireOp",EDGE,"E31.right"),sQuery(id+"F0.wireOp",EDGE,"E32.top"),sQuery(id+"F0.wireOp",EDGE,"E33.right"),sQuery(id+"F0.wireOp",EDGE,"E33.top"),sQuery(id+"F0.wireOp",EDGE,"E34.left"),sQuery(id+"F0.wireOp",EDGE,"E34.top"),sQuery(id+"F0.wireOp",EDGE,"E35.right"),sQuery(id+"F0.wireOp",EDGE,"E35.top"),sQuery(id+"F0.wireOp",EDGE,"E36.left"),sQuery(id+"F0.wireOp",EDGE,"E36.top"),sQuery(id+"F0.wireOp",EDGE,"E37.right"),sQuery(id+"F0.wireOp",EDGE,"E37.top"),sQuery(id+"F0.wireOp",EDGE,"E39.bottom"),sQuery(id+"F0.wireOp",EDGE,"E40.top"),sQuery(id+"F0.wireOp",EDGE,"E39.right"),sQuery(id+"F0.wireOp",EDGE,"E41.bottom"),sQuery(id+"F0.wireOp",EDGE,"E40.right"),sQuery(id+"F0.wireOp",EDGE,"E42.top"),sQuery(id+"F0.wireOp",EDGE,"E41.right"),sQuery(id+"F0.wireOp",EDGE,"E43.bottom"),sQuery(id+"F0.wireOp",EDGE,"E43.right"),sQuery(id+"F0.wireOp",EDGE,"E43.top"),sQuery(id+"F0.wireOp",EDGE,"E44.left"),sQuery(id+"F0.wireOp",EDGE,"E44.top"),sQuery(id+"F0.wireOp",EDGE,"E45.right"),sQuery(id+"F0.wireOp",EDGE,"E45.top"),sQuery(id+"F0.wireOp",EDGE,"E46.left"),sQuery(id+"F0.wireOp",EDGE,"E46.top"),sQuery(id+"F0.wireOp",EDGE,"E47.right"),sQuery(id+"F0.wireOp",EDGE,"E48.bottom"),sQuery(id+"F0.wireOp",EDGE,"E42.right"),sQuery(id+"F0.wireOp",EDGE,"E47.top")])]});
            deleteBodies(context, id + "F6", {"entities" : qUnion([Q0, Q1])});
        }
        {
            var Q0;
            Q0=makeQuery(id+"F1.opExtrude","CAP_FACE",FACE,{"disambiguationData":[OSD([sQuery(id+"F0.wireOp",EDGE,"E2.top"),sQuery(id+"F0.wireOp",EDGE,"E3.bottom"),sQuery(id+"F0.wireOp",EDGE,"E2.right"),sQuery(id+"F0.wireOp",EDGE,"E4.top"),sQuery(id+"F0.wireOp",EDGE,"E3.right"),sQuery(id+"F0.wireOp",EDGE,"E5.bottom"),sQuery(id+"F0.wireOp",EDGE,"E4.right"),sQuery(id+"F0.wireOp",EDGE,"E6.top"),sQuery(id+"F0.wireOp",EDGE,"E5.right"),sQuery(id+"F0.wireOp",EDGE,"E8.right"),sQuery(id+"F0.wireOp",EDGE,"E8.top"),sQuery(id+"F0.wireOp",EDGE,"E9.left"),sQuery(id+"F0.wireOp",EDGE,"E9.top"),sQuery(id+"F0.wireOp",EDGE,"E10.right"),sQuery(id+"F0.wireOp",EDGE,"E10.top"),sQuery(id+"F0.wireOp",EDGE,"E11.left"),sQuery(id+"F0.wireOp",EDGE,"E11.top"),sQuery(id+"F0.wireOp",EDGE,"E12.right"),sQuery(id+"F0.wireOp",EDGE,"E14.bottom"),sQuery(id+"F0.wireOp",EDGE,"E15.top"),sQuery(id+"F0.wireOp",EDGE,"E14.right"),sQuery(id+"F0.wireOp",EDGE,"E16.bottom"),sQuery(id+"F0.wireOp",EDGE,"E15.right"),sQuery(id+"F0.wireOp",EDGE,"E17.top"),sQuery(id+"F0.wireOp",EDGE,"E16.right"),sQuery(id+"F0.wireOp",EDGE,"E18.left"),sQuery(id+"F0.wireOp",EDGE,"E18.top"),sQuery(id+"F0.wireOp",EDGE,"E19.right"),sQuery(id+"F0.wireOp",EDGE,"E19.top"),sQuery(id+"F0.wireOp",EDGE,"E20.left"),sQuery(id+"F0.wireOp",EDGE,"E20.top"),sQuery(id+"F0.wireOp",EDGE,"E21.right"),sQuery(id+"F0.wireOp",EDGE,"E22.bottom"),sQuery(id+"F0.wireOp",EDGE,"E22.right"),sQuery(id+"F0.wireOp",EDGE,"E24.bottom"),sQuery(id+"F0.wireOp",EDGE,"E17.right")])],"isStart":false});
            var sketch = newSketch(context, id + "F7", { "sketchPlane" : qUnion([Q0])});
            skText(sketch, "E58", { "text": "0", "fontName": "NotoSerif-Bold.ttf"});
            const initialGuessF7  = {"E58": [-0.01482, -0.0132, 1, 0, 0.02915]};
            skSetInitialGuess(sketch, initialGuessF7);
            skSolve(sketch);
        }
        {
            var Q0;
            Q0 = qSketchRegion(id + "F7", true);
            extrude(context, id + "F8", {"entities" : qUnion([Q0]), "operationType" : NewBodyOperationType.ADD, "depth" : 1.27 * mm});
        }
    });
